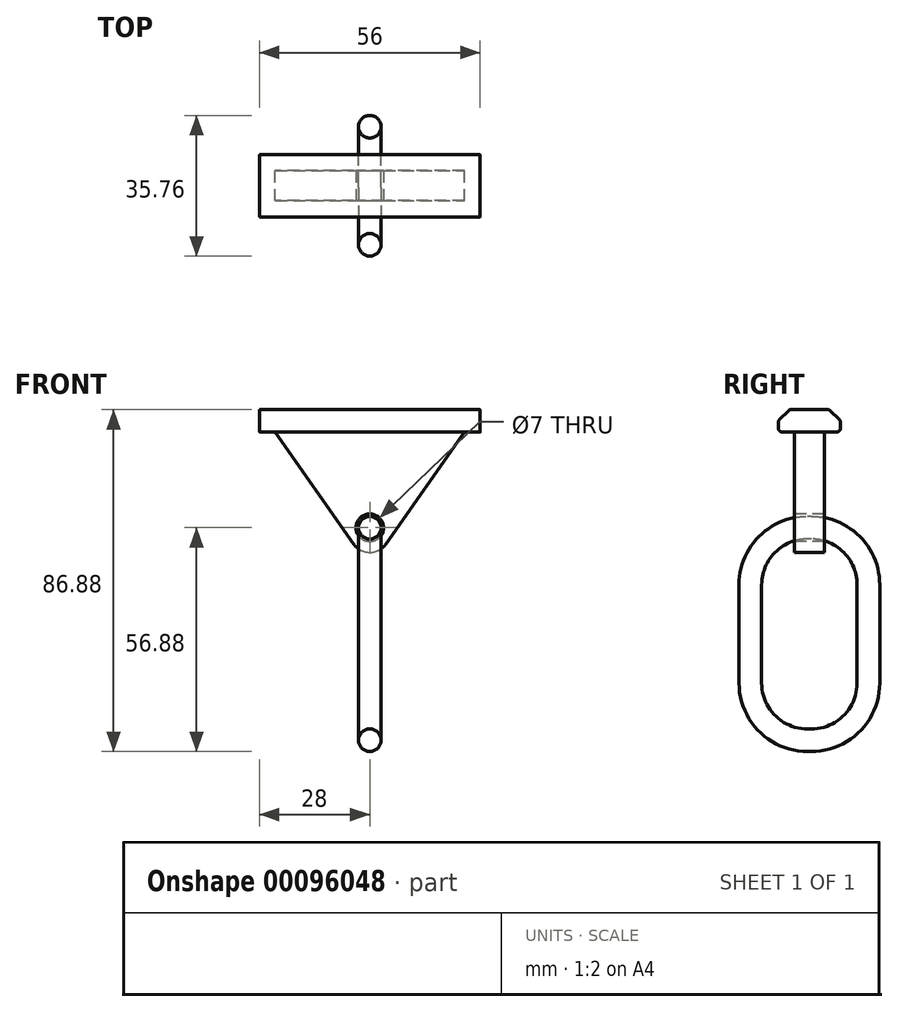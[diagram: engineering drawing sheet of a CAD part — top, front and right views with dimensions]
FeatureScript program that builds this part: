
annotation { "Feature Type Name" : "Feature", "Feature Type Description" : "" }
export const myFeature = defineFeature(function(context is Context, id is Id, definition is map)
    precondition{}
    {
        {
            var Q0;
            Q0=qCreatedBy(makeId("Right.planeOp"),FACE);
            var sketch = newSketch(context, id + "F0", { "sketchPlane" : qUnion([Q0])});
            skLineSegment(sketch, "E0", {"start": v(-5.05, 0) * mm, "end": v(5.05, 0) * mm});
            skLineSegment(sketch, "E1", {"start": v(-7.9, -5.7) * mm, "end": v(7.9, -5.7) * mm});
            skLineSegment(sketch, "E2", {"start": v(0, 0) * mm, "end": v(0, -5.7) * mm});
            skLineSegment(sketch, "E3", {"start": v(-7.9, -5.7) * mm, "end": v(-7.9, -2.85) * mm});
            skLineSegment(sketch, "E4", {"start": v(7.9, -5.7) * mm, "end": v(7.9, -2.85) * mm});
            skLineSegment(sketch, "E5", {"start": v(7.9, -2.85) * mm, "end": v(5.05, 0) * mm});
            skLineSegment(sketch, "E6", {"start": v(-7.9, -2.85) * mm, "end": v(-5.05, 0) * mm});
            skSolve(sketch);
        }
        {
            var Q0;
            Q0=qSketchRegion(id+"F0",true);
            extrude(context, id + "F1", {"entities" : qUnion([Q0]), "endBound" : BoundingType.SYMMETRIC, "depth" : 56 * mm});
        }
        {
            var Q0;
            Q0=makeQuery(id+"F1.opExtrude","SWEPT_EDGE",EDGE,{"disambiguationData":[OSD([sQuery(id+"F0.wireOp",EDGE,"E0"),sQuery(id+"F0.wireOp",EDGE,"E6")])]});
            var Q1;
            Q1=makeQuery(id+"F1.opExtrude","SWEPT_EDGE",EDGE,{"disambiguationData":[OSD([sQuery(id+"F0.wireOp",EDGE,"E3"),sQuery(id+"F0.wireOp",EDGE,"E6")])]});
            var Q2;
            Q2=makeQuery(id+"F1.opExtrude","SWEPT_EDGE",EDGE,{"disambiguationData":[OSD([sQuery(id+"F0.wireOp",EDGE,"E1"),sQuery(id+"F0.wireOp",EDGE,"E3")])]});
            var Q3;
            Q3=makeQuery(id+"F1.opExtrude","SWEPT_EDGE",EDGE,{"disambiguationData":[OSD([sQuery(id+"F0.wireOp",EDGE,"E0"),sQuery(id+"F0.wireOp",EDGE,"E5")])]});
            var Q4;
            Q4=makeQuery(id+"F1.opExtrude","SWEPT_EDGE",EDGE,{"disambiguationData":[OSD([sQuery(id+"F0.wireOp",EDGE,"E4"),sQuery(id+"F0.wireOp",EDGE,"E5")])]});
            var Q5;
            Q5=makeQuery(id+"F1.opExtrude","SWEPT_EDGE",EDGE,{"disambiguationData":[OSD([sQuery(id+"F0.wireOp",EDGE,"E1"),sQuery(id+"F0.wireOp",EDGE,"E4")])]});
            fillet(context, id + "F2", {"entities" : qUnion([Q0, Q1, Q2, Q3, Q4, Q5]), "radius" : 1 * mm, "tangentPropagation" : true, "allowEdgeOverflow" : false});
        }
        {
            var Q0;
            Q0=qCreatedBy(makeId("Front.planeOp"),FACE);
            var sketch = newSketch(context, id + "F3", { "sketchPlane" : qUnion([Q0])});
            skLineSegment(sketch, "E7", {"start": v(-24.02, -5.7) * mm, "end": v(24.02, -5.7) * mm});
            skLineSegment(sketch, "E8", {"start": v(24.02, -5.7) * mm, "end": v(0, -40) * mm});
            skLineSegment(sketch, "E9", {"start": v(0, -40) * mm, "end": v(-24.02, -5.7) * mm});
            skSolve(sketch);
        }
        {
            var Q0;
            Q0=qSketchRegion(id+"F3",true);
            extrude(context, id + "F4", {"entities" : qUnion([Q0]), "operationType" : NewBodyOperationType.ADD, "endBound" : BoundingType.SYMMETRIC, "depth" : 7.6 * mm});
        }
        {
            var Q0;
            Q0=makeQuery(id+"F4.opExtrude","SWEPT_EDGE",EDGE,{"disambiguationData":[OSD([sQuery(id+"F3.wireOp",EDGE,"E8"),sQuery(id+"F3.wireOp",EDGE,"E9")])]});
            fillet(context, id + "F5", {"entities" : qUnion([Q0]), "radius" : 5 * mm, "tangentPropagation" : true, "allowEdgeOverflow" : false});
        }
        {
            var Q0;
            Q0=qCreatedBy(makeId("Front.planeOp"),FACE);
            var sketch = newSketch(context, id + "F6", { "sketchPlane" : qUnion([Q0])});
            skCircle(sketch, "E10", {"center": v(0, -30) * mm, "radius": 3.5 * mm});
            skSolve(sketch);
        }
        {
            var Q0;
            Q0=qSketchRegion(id+"F6",true);
            extrude(context, id + "F7", {"entities" : qUnion([Q0]), "operationType" : NewBodyOperationType.REMOVE, "endBound" : BoundingType.SYMMETRIC, "oppositeDirection" : true, "depth" : 25 * mm});
        }
        {
            var Q0;
            Q0=qCreatedBy(makeId("Right.planeOp"),FACE);
            var sketch = newSketch(context, id + "F8", { "sketchPlane" : qUnion([Q0])});
            skLineSegment(sketch, "E11.bottom", {"start": v(-0.5, -30) * mm, "end": v(0.5, -30) * mm});
            skLineSegment(sketch, "E11.top", {"start": v(-0.5, -84) * mm, "end": v(0.5, -84) * mm});
            skLineSegment(sketch, "E11.left", {"start": v(-15, -44.5) * mm, "end": v(-15, -69.5) * mm});
            skLineSegment(sketch, "E11.right", {"start": v(15, -44.5) * mm, "end": v(15, -69.5) * mm});
            skPoint(sketch, "E12.visualSharp", {"position": v(-15, -30) * mm});
            skArc(sketch, "E12.filletArc", {"start": v(-0.5, -30) * mm, "mid": v(-10.75, -34.25) * mm, "end": v(-15, -44.5) * mm});
            skPoint(sketch, "E13.visualSharp", {"position": v(15, -30) * mm});
            skArc(sketch, "E13.filletArc", {"start": v(15, -44.5) * mm, "mid": v(10.75, -34.25) * mm, "end": v(0.5, -30) * mm});
            skPoint(sketch, "E14.visualSharp", {"position": v(-15, -84) * mm});
            skArc(sketch, "E14.filletArc", {"start": v(-15, -69.5) * mm, "mid": v(-10.75, -79.75) * mm, "end": v(-0.5, -84) * mm});
            skPoint(sketch, "E15.visualSharp", {"position": v(15, -84) * mm});
            skArc(sketch, "E15.filletArc", {"start": v(0.5, -84) * mm, "mid": v(10.75, -79.75) * mm, "end": v(15, -69.5) * mm});
            skSolve(sketch);
        }
        {
            var Q0;
            Q0=qCreatedBy(makeId("Front.planeOp"),FACE);
            var sketch = newSketch(context, id + "F9", { "sketchPlane" : qUnion([Q0])});
            skCircle(sketch, "E16", {"center": v(0, -30) * mm, "radius": 2.88 * mm});
            skSolve(sketch);
        }
        {
            var Q0;
            Q0=qSketchRegion(id+"F9",true);
            var Q1;
            Q1=qConstructionFilter(qBodyType(qCreatedBy(id+"F8",EDGE),BodyType.WIRE),ConstructionObject.NO);
            sweep(context, id + "F10", {"operationType" : NewBodyOperationType.ADD, "profiles" : qUnion([Q0]), "path" : qUnion([Q1])});
        }
    });
